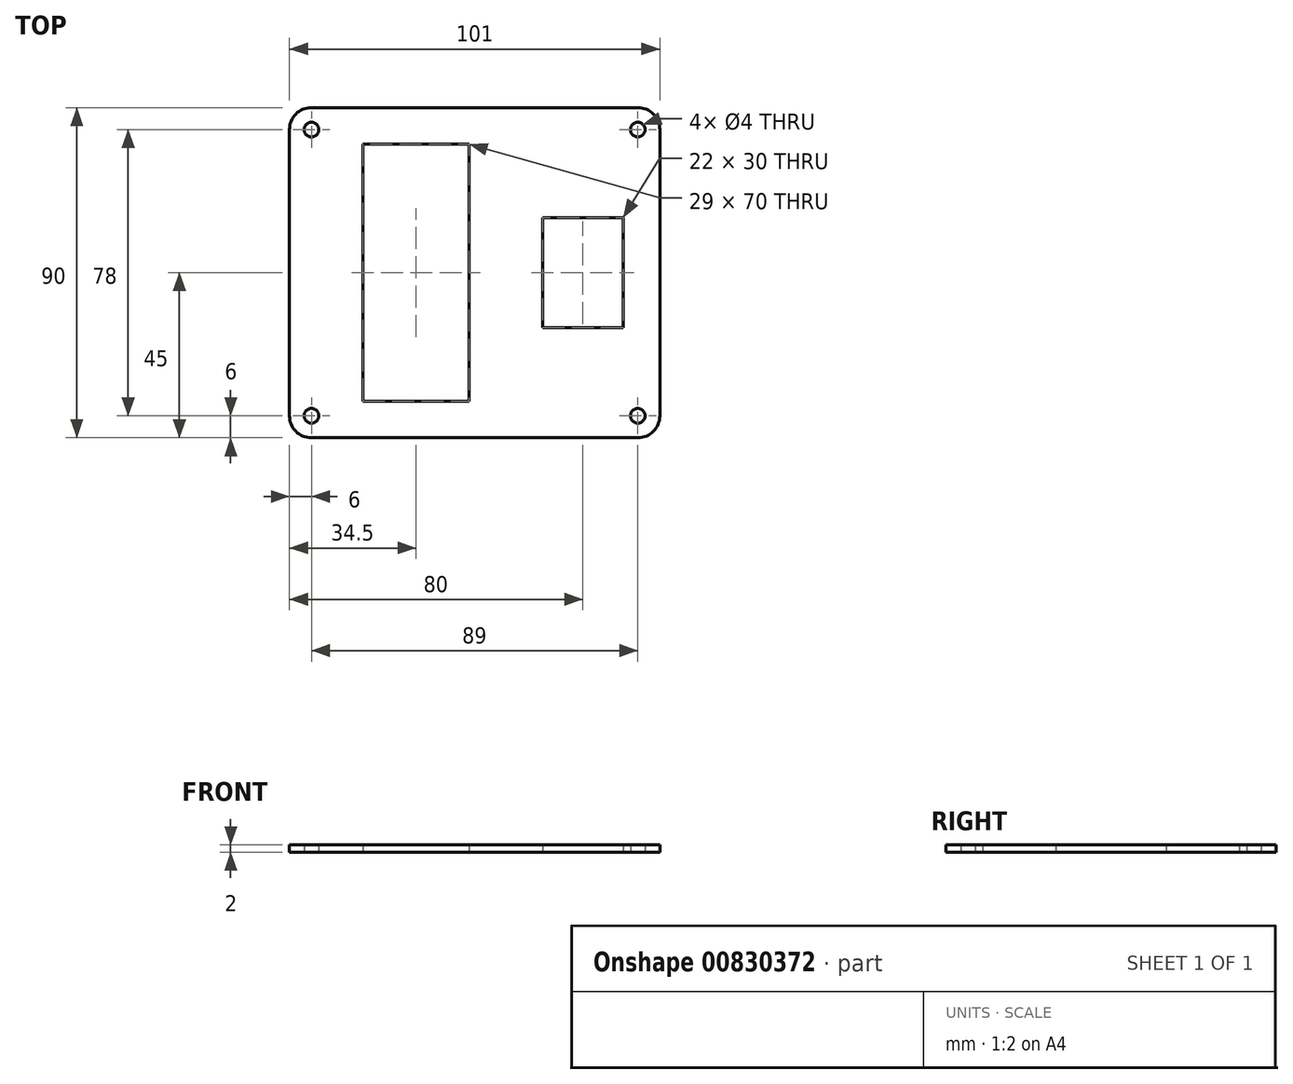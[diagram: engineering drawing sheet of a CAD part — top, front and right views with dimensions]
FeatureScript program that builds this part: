
annotation { "Feature Type Name" : "Feature", "Feature Type Description" : "" }
export const myFeature = defineFeature(function(context is Context, id is Id, definition is map)
    precondition{}
    {
        {
            var Q0;
            Q0=qCreatedBy(makeId("Top.planeOp"),FACE);
            var sketch = newSketch(context, id + "F0", { "sketchPlane" : qUnion([Q0])});
            skLineSegment(sketch, "E0.bottom", {"start": v(-6, 0) * mm, "end": v(-95, 0) * mm});
            skLineSegment(sketch, "E0.top", {"start": v(-6, 90) * mm, "end": v(-95, 90) * mm});
            skLineSegment(sketch, "E0.left", {"start": v(0, 6) * mm, "end": v(0, 84) * mm});
            skLineSegment(sketch, "E0.right", {"start": v(-101, 6) * mm, "end": v(-101, 84) * mm});
            skPoint(sketch, "E1.visualSharp", {"position": v(-101, 90) * mm});
            skArc(sketch, "E1.filletArc", {"start": v(-95, 90) * mm, "mid": v(-99.24, 88.24) * mm, "end": v(-101, 84) * mm});
            skPoint(sketch, "E2.visualSharp", {"position": v(0, 90) * mm});
            skArc(sketch, "E2.filletArc", {"start": v(0, 84) * mm, "mid": v(-1.76, 88.24) * mm, "end": v(-6, 90) * mm});
            skPoint(sketch, "E3.visualSharp", {"position": v(0, 0) * mm});
            skArc(sketch, "E3.filletArc", {"start": v(-6, 0) * mm, "mid": v(-1.76, 1.76) * mm, "end": v(0, 6) * mm});
            skPoint(sketch, "E4.visualSharp", {"position": v(-101, 0) * mm});
            skArc(sketch, "E4.filletArc", {"start": v(-101, 6) * mm, "mid": v(-99.24, 1.76) * mm, "end": v(-95, 0) * mm});
            skLineSegment(sketch, "E5.bottom", {"start": v(-81, 80) * mm, "end": v(-52, 80) * mm});
            skLineSegment(sketch, "E5.top", {"start": v(-81, 10) * mm, "end": v(-52, 10) * mm});
            skLineSegment(sketch, "E5.left", {"start": v(-81, 80) * mm, "end": v(-81, 10) * mm});
            skLineSegment(sketch, "E5.right", {"start": v(-52, 80) * mm, "end": v(-52, 10) * mm});
            skLineSegment(sketch, "E6.bottom", {"start": v(-32, 60) * mm, "end": v(-10, 60) * mm});
            skLineSegment(sketch, "E6.top", {"start": v(-32, 30) * mm, "end": v(-10, 30) * mm});
            skLineSegment(sketch, "E6.left", {"start": v(-32, 60) * mm, "end": v(-32, 30) * mm});
            skLineSegment(sketch, "E6.right", {"start": v(-10, 60) * mm, "end": v(-10, 30) * mm});
            skCircle(sketch, "E7", {"center": v(-95, 84) * mm, "radius": 2 * mm});
            skCircle(sketch, "E8", {"center": v(-6, 84) * mm, "radius": 2 * mm});
            skCircle(sketch, "E9", {"center": v(-95, 6) * mm, "radius": 2 * mm});
            skCircle(sketch, "E10", {"center": v(-6, 6) * mm, "radius": 2 * mm});
            skSolve(sketch);
        }
        {
            var Q0;
            Q0 = qSketchRegion(id + "F0", true);
            extrude(context, id + "F1", {"entities" : qUnion([Q0]), "depth" : 2 * mm, "offsetDistance" : 25 * mm});
        }
    });
